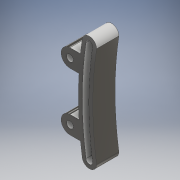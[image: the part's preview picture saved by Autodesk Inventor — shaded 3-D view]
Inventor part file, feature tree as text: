
AUTODESK INVENTOR PART (.ipt)
format: ipt  version: 2017 (Build 210142000, 142)  size: 188,928 bytes
history: native  units: mm
features: extrude x2, chamfer x2, sketch x2, projected_geometry x1
ambient origin geometry x8: Origin, YZ Plane, XZ Plane, XY Plane, X Axis, Y Axis, Z Axis, Center Point
bodies: Body1 (feature_tree)
feature tree (7):
  extrude  "Extrusion2"  Depth=156.215396mm
  extrude  "Extrusion3"  Depth=153.0mm
  chamfer  "Chamfer1"  Distance=151.516469mm
  chamfer  "Chamfer2"  Distance=149.786097mm
  sketch  "Sketch1"  dims[d0=3.0mm d1=6.5mm d3=8.0mm d4=156.215396mm]
  sketch  "Sketch2"  dims[d5=154.483849mm d6=153.0mm d7=151.516469mm d8=149.786097mm d9=17.922963mm d10=13.538519mm d11=13.538519mm d12=31.461481mm d13=13.538519mm d14=31.461481mm d15=10.28254mm d16=32.632503mm d17=14.305616mm d20=10.0mm d21=0.0mm d22=6.5mm d23=6.5mm d24=1.75mm d25=0.0mm d26=1.75mm d27=2.0mm d28=45.0deg d29=1.75mm d30=2.0mm d31=45.0deg]
  projected_geometry  "Projected Loop1"
